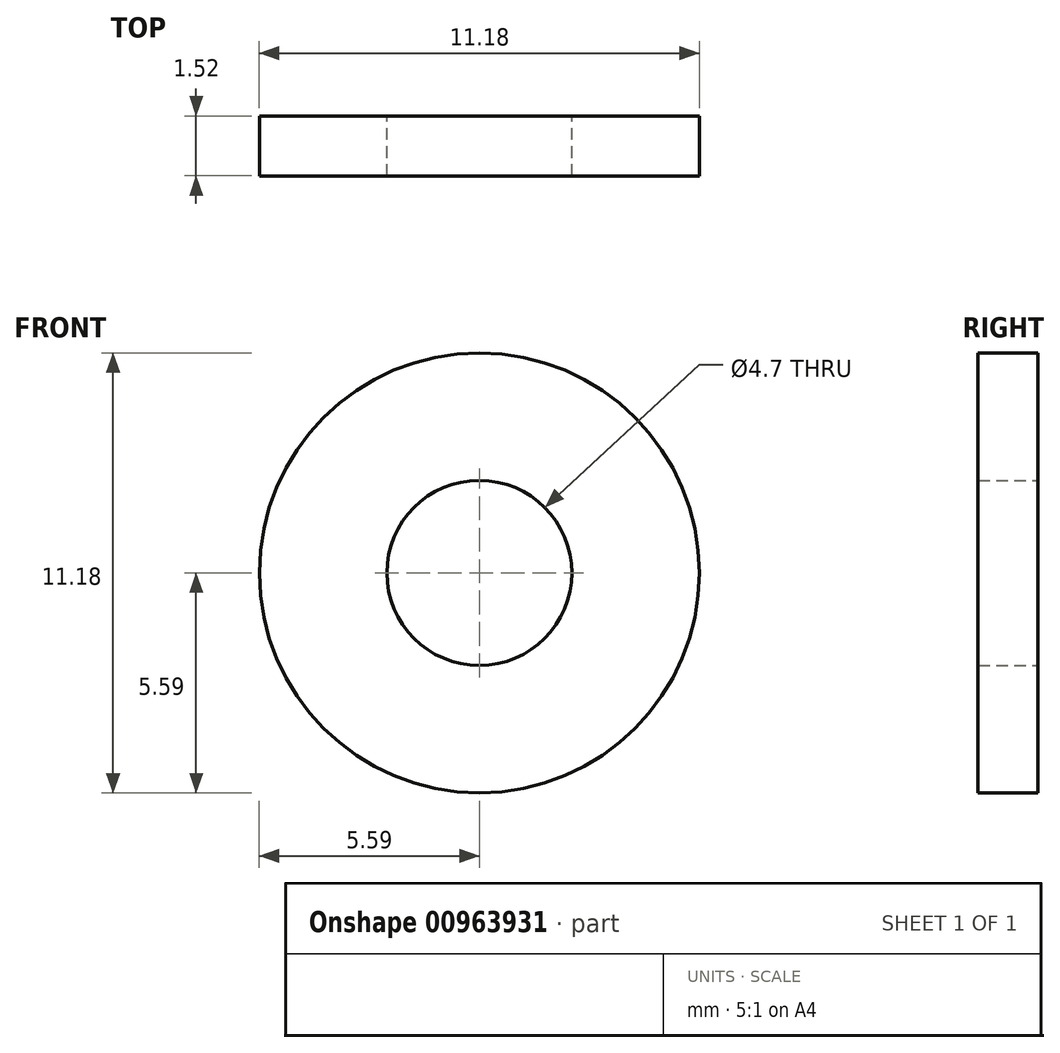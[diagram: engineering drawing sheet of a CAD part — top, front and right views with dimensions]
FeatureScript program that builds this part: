
annotation { "Feature Type Name" : "Feature", "Feature Type Description" : "" }
export const myFeature = defineFeature(function(context is Context, id is Id, definition is map)
    precondition{}
    {
        {
            var Q0;
            Q0=qCreatedBy(makeId("Front.planeOp"),FACE);
            var sketch = newSketch(context, id + "F0", { "sketchPlane" : qUnion([Q0])});
            skCircle(sketch, "E0", {"center": v(0, 0) * mm, "radius": 5.59 * mm});
            skCircle(sketch, "E1", {"center": v(0, 0) * mm, "radius": 2.35 * mm});
            skSolve(sketch);
        }
        {
            var Q0;
            Q0=makeQuery(id+"F0.imprint","IMPRINT",FACE,{"disambiguationData":[TD([[makeQuery(id+"F0.imprint","IMPRINT",EDGE,{"derivedFrom":sQuery(id+"F0.wireOp",EDGE,"E0")}),1.0]])]});
            extrude(context, id + "F1", {"entities" : qUnion([Q0]), "depth" : 1.52 * mm, "offsetDistance" : 25.4 * mm});
        }
    });
